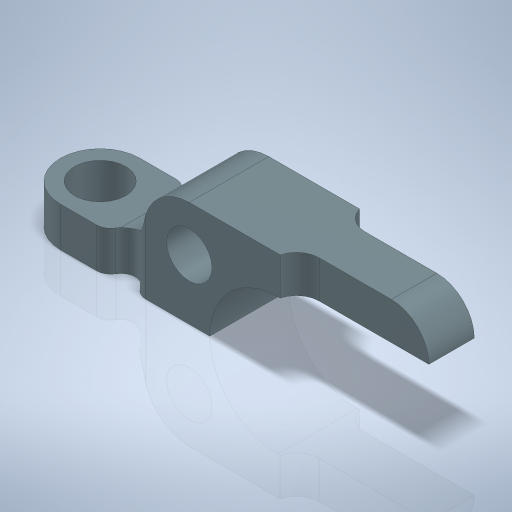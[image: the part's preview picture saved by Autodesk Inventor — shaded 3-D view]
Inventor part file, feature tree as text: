
AUTODESK INVENTOR PART (.ipt)
format: ipt  version: 2024 (Build 280153000, 153)  size: 337,920 bytes
history: native  units: mm
features: sketch x5, extrude x3, fillet x3, projected_geometry x3, hole x2, mirror x2, plane x1
ambient origin geometry x8: Origin, YZ Plane, XZ Plane, XY Plane, X Axis, Y Axis, Z Axis, Center Point
bodies: Volumenkörper1 (feature_tree)
feature tree (19):
  extrude  "Extrusion1"  Depth=4.0mm
  hole  "Bohrung1"  [1 undecoded]
  extrude  "Extrusion2"  Depth=6.0mm
  fillet  "Rundung1"  Radius=14.85mm
  plane  "Arbeitsebene1"
  mirror  "Spiegeln1"
  fillet  "Rundung2"  Radius=19.6mm
  hole  "Bohrung2"  [1 undecoded]
  extrude  "Extrusion5"  Depth=6.0mm
  mirror  "Spiegeln2"
  fillet  "Rundung3"  Radius=7.0mm
  sketch  "Skizze1"  dims[d0=3.0mm d1=4.0mm]
  sketch  "Skizze3"  dims[d2=3.5mm d3=7.8mm]
  sketch  "Skizze4"  dims[d4=3.3mm d5=6.0mm d6=14.85mm d7=19.6mm]
  projected_geometry  "Projizierte Kontur3"
  sketch  "Skizze5"  dims[d8=7.0mm d9=0.0mm]
  sketch  "Skizze6"  dims[d10=4.0mm d11=6.0mm d12=4.0mm d13=2.0mm d14=90.0deg d15=8.0mm d16=0.0mm d17=1.25mm d18=6.0mm d19=7.0mm d20=0.0mm d21=1.25mm d22=3.5mm d23=3.5mm d24=4.5mm d25=6.0mm d26=4.0mm d27=2.0mm d28=90.0deg d29=8.0mm d30=0.0mm d32=1.5mm d38=8.0mm d39=10.0mm d40=0.0mm d41=2.0mm d34=0.5mm d35=0.872665mm d36=0.5mm d37=0.872665mm]
  projected_geometry  "Projizierte Kontur4"
  projected_geometry  "Projizierte Kontur5"
note: 2 required parameter values undecoded (feature->parameter linkage not recoverable at this tier; creation-order binding heuristic only, values carry confidence <= 0.55)
